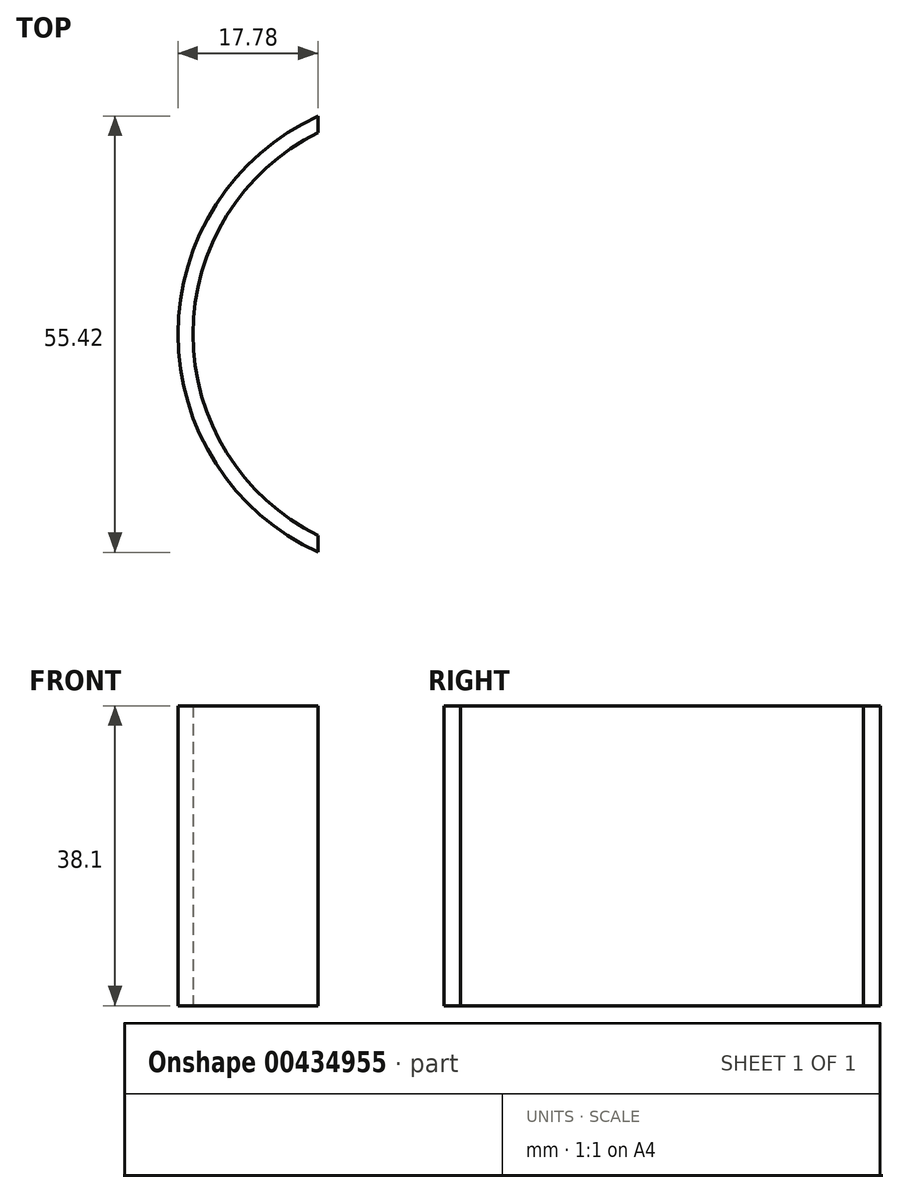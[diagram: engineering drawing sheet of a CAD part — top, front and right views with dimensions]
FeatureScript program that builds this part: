
annotation { "Feature Type Name" : "Feature", "Feature Type Description" : "" }
export const myFeature = defineFeature(function(context is Context, id is Id, definition is map)
    precondition{}
    {
        {
            var Q0;
            Q0=qCreatedBy(makeId("Top.planeOp"),FACE);
            var sketch = newSketch(context, id + "F0", { "sketchPlane" : qUnion([Q0])});
            skArc(sketch, "E0", {"start": v(-12.7, 25.6) * mm, "mid": v(-28.57, 0) * mm, "end": v(-12.7, -25.6) * mm});
            skLineSegment(sketch, "E1", {"start": v(12.7, 25.6) * mm, "end": v(12.7, 27.7) * mm});
            skLineSegment(sketch, "E2", {"start": v(12.7, 27.7) * mm, "end": v(12.7, 25.6) * mm});
            skLineSegment(sketch, "E3", {"start": v(-12.7, 25.6) * mm, "end": v(-12.7, 27.7) * mm});
            skLineSegment(sketch, "E4", {"start": v(-12.7, 27.7) * mm, "end": v(-12.7, 25.6) * mm});
            skArc(sketch, "E5.trimOffspring", {"start": v(12.7, -25.6) * mm, "mid": v(28.58, 0) * mm, "end": v(12.7, 25.6) * mm});
            skArc(sketch, "E6", {"start": v(-12.7, 27.7) * mm, "mid": v(-30.48, 0) * mm, "end": v(-12.7, -27.7) * mm});
            skArc(sketch, "E7.trimOffspring", {"start": v(12.7, -27.7) * mm, "mid": v(30.48, 0) * mm, "end": v(12.7, 27.7) * mm});
            skLineSegment(sketch, "E8.trimOffspring", {"start": v(12.7, -25.6) * mm, "end": v(12.7, -27.7) * mm});
            skLineSegment(sketch, "E9.trimOffspring", {"start": v(-12.7, -25.6) * mm, "end": v(-12.7, -27.7) * mm});
            skPoint(sketch, "E10.orphan", {"position": v(12.7, 0) * mm});
            skSolve(sketch);
        }
        {
            var Q0;
            Q0=makeQuery(id+"F0.imprint","IMPRINT",FACE,{"disambiguationData":[TD([[makeQuery(id+"F0.imprint","IMPRINT",EDGE,{"derivedFrom":sQuery(id+"F0.wireOp",EDGE,"E0")}),-1.0]])]});
            var Q1;
            Q1=makeQuery(id+"F0.imprint","IMPRINT",FACE,{"disambiguationData":[TD([[makeQuery(id+"F0.imprint","IMPRINT",EDGE,{"derivedFrom":sQuery(id+"F0.wireOp",EDGE,"E2")}),1.0]])]});
            extrude(context, id + "F1", {"entities" : qUnion([Q0, Q1]), "depth" : 38.1 * mm});
        }
    });
